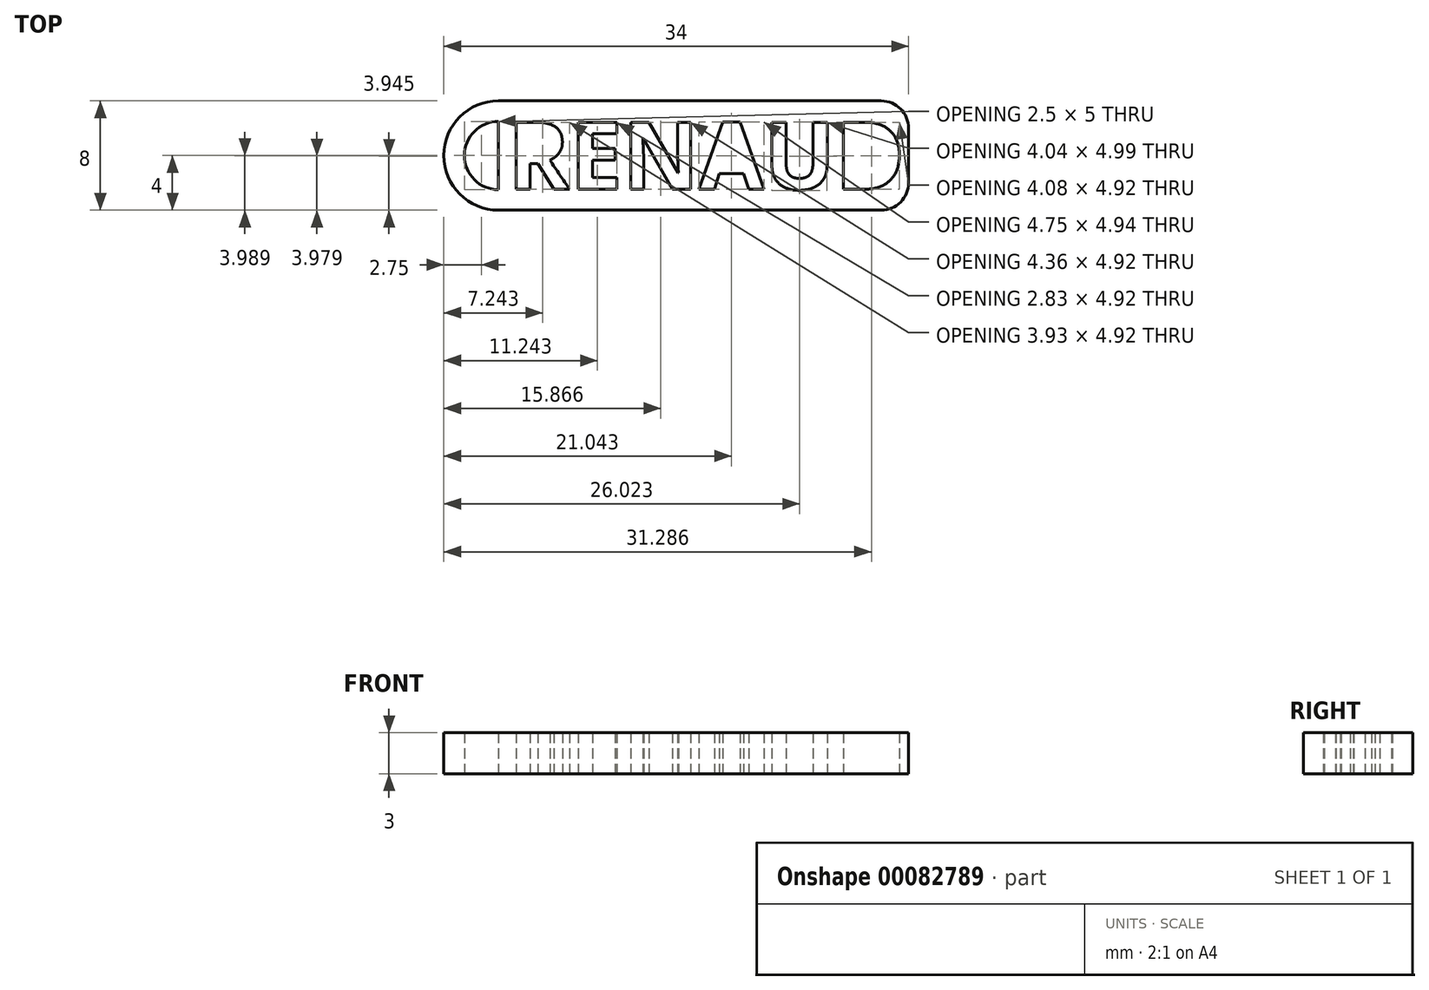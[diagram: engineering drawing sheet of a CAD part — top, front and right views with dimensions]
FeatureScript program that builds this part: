
annotation { "Feature Type Name" : "Feature", "Feature Type Description" : "" }
export const myFeature = defineFeature(function(context is Context, id is Id, definition is map)
    precondition{}
    {
        {
            var Q0;
            Q0=qCreatedBy(makeId("Top.planeOp"),FACE);
            var sketch = newSketch(context, id + "F0", { "sketchPlane" : qUnion([Q0])});
            skLineSegment(sketch, "E0.bottom", {"start": v(-15, 4) * mm, "end": v(13, 4) * mm});
            skLineSegment(sketch, "E0.top", {"start": v(-15, -4) * mm, "end": v(13, -4) * mm});
            skLineSegment(sketch, "E0.left", {"start": v(-15, 4) * mm, "end": v(-15, -4) * mm});
            skLineSegment(sketch, "E0.right", {"start": v(15, 2) * mm, "end": v(15, -2) * mm});
            skPoint(sketch, "E0.middle", {"position": v(0, 0) * mm});
            skArc(sketch, "E1", {"start": v(-15, 4) * mm, "mid": v(-19, 0) * mm, "end": v(-15, -4) * mm});
            skArc(sketch, "E2.0", {"start": v(-15, 2.5) * mm, "mid": v(-17.5, 0) * mm, "end": v(-15, -2.5) * mm});
            skPoint(sketch, "E3.center.orphan", {"position": v(15, 0) * mm});
            skPoint(sketch, "E4.visualSharp", {"position": v(15, 4) * mm});
            skArc(sketch, "E4.filletArc", {"start": v(15, 2) * mm, "mid": v(14.41, 3.41) * mm, "end": v(13, 4) * mm});
            skPoint(sketch, "E5.visualSharp", {"position": v(15, -4) * mm});
            skArc(sketch, "E5.filletArc", {"start": v(13, -4) * mm, "mid": v(14.41, -3.41) * mm, "end": v(15, -2) * mm});
            skText(sketch, "E6", { "text": "RENAUD", "fontName": "OpenSans-Bold.ttf"});
            const initialGuessF0  = {"E6": [-0.01434, -0.00248, 1, 0, 0.00496]};
            skSetInitialGuess(sketch, initialGuessF0);
            skSolve(sketch);
        }
        {
            var Q0;
            Q0=makeQuery(id+"F0.imprint","IMPRINT",FACE,{"disambiguationData":[TD([[makeQuery(id+"F0.imprint","IMPRINT",EDGE,{"derivedFrom":sQuery(id+"F0.wireOp",EDGE,"E0.left")}),-1.0]])]});
            var Q1;
            {var subQ1=sQuery(id+"F0.wireOp",EDGE,"E0.bottom");Q1=makeQuery(id+"F0.imprint","IMPRINT",FACE,{"disambiguationData":[TD([[makeQuery(id+"F0.imprint","IMPRINT",EDGE,{"derivedFrom":subQ1}),-1.0]])]});}
            var Q2;
            {var subQ0=sQuery(id+"F0.wireOp",EDGE,"E3");Q2=makeQuery(id+"F0.imprint","IMPRINT",FACE,{"disambiguationData":[TD([[makeQuery(id+"F0.imprint","IMPRINT",EDGE,{"derivedFrom":subQ0}),-1.0]])]});}
            extrude(context, id + "F1", {"entities" : qUnion([Q0, Q1, Q2]), "depth" : 3 * mm});
        }
    });
